# Revit family: Hager-Univers-IP30-sistema-A_parete-CH-it
name_source: partatom
category: Electrical Equipment
units: mm (PartAtom-declared; Revit-internal decimal feet)

## family parameters
Cut with Voids When Loaded = No
Host = Face
Panel Configuration = Two Columns, Circuits Across
Part Type = Panelboard
Room Calculation Point = No
Round Connector Dimension = Use Diameter
Shared = No

## types (20) — shared parameters
EF000003 - Tipo di montaggio = EV000384 - A parete
EF000007 - colore = EV000202 - bianco
EF000049 - profondità = 161 mm  [stored 0.528215 ft]
EF000116 - numero RAL = 9010
EF000118 - con piastra di montaggio = No
EF000339 - tipo di copertura = EV000494 - senza
EF001062 - esecuzione EMC = No
EF001088 - possibilità di applicazione = Yes
EF001131 - profondità interna = 161 mm  [stored 0.528215 ft]
EF001134 - barra DIN = Yes
EF001596 - Attacco Lampada = EV000179 - acciaio
EF002950 - Numero moduli DIN = 12
EF004462 - tipo di chiusura = EV000154 - altri
EF005474 - grado di protezione (IP) = EV006410 - IP30
EF006244 - coperchio/porta trasparente = No
EF006306 - con serratura = No
EF009212 - esecuzione coperchio = EV009916 - con taglio
EF015776 - Morsettiera di terra = Yes
EF015777 - Morsettiera neutra = Yes
EF015941 - Segnale di passaggio porta = No
HG000002 - Con porta = No
HG000003 - Gamma = Univers
HG000005 - Spessore = 3 mm  [stored 0.00984252 ft]
HG000006 - Ad incasso = No
HG000009 - Porta doppia a battente = No
HG000010 - Porte asimmetriche = No
HG000011 - File vuote nella parte basse = No
HG000017 - Distanza tra i poli = 18 mm  [stored 0.0590551 ft]
Manufacturer = Hager
Type Comments = Univers
zero-valued in all types: Default Elevation, EF000218 - profondità di incasso, EF000332 - Altezza della parte incassata, EF000846 - larghezza di montaggio, HG000007 - Numero di colonne vuote, HG000008 - Numero di file vuote

## per-type parameters (varying)
| type | EF000008 - Larghezza | EF000040 - Altezza | EF000266 - numero di file | HG000001 - Numero di colonne | HG000004 - Codice produttore | Model |
| A parete IP30 L1050 A1100 P161 12 Unità di divisione - FWB74T1S | 1050 mm | 1100 mm | 28 | 4 | FWB74T1S | FWB74T1S |
| A parete IP30 L1050 A500 P161 12 Unità di divisione - FWB34T1S | 1050 mm | 500 mm  [stored 1.64042 ft] | 12 | 4 | FWB34T1S | FWB34T1S |
| A parete IP30 L1050 A650 P161 12 Unità di divisione - FWB44T1S | 1050 mm | 650 mm  [stored 2.13255 ft] | 16 | 4 | FWB44T1S | FWB44T1S |
| A parete IP30 L1050 A800 P161 12 Unità di divisione - FWB54T1S | 1050 mm | 800 mm  [stored 2.62467 ft] | 20 | 4 | FWB54T1S | FWB54T1S |
| A parete IP30 L1050 A950 P161 12 Unità di divisione - FWB64T1S | 1050 mm | 950 mm  [stored 3.1168 ft] | 24 | 4 | FWB64T1S | FWB64T1S |
| A parete IP30 L300 A1100 P161 12 Unità di divisione - FWB71T1S | 300 mm | 1100 mm | 7 | 1 | FWB71T1S | FWB71T1S |
| A parete IP30 L300 A500 P161 12 Unità di divisione - FWB31T1S | 300 mm | 500 mm  [stored 1.64042 ft] | 3 | 1 | FWB31T1S | FWB31T1S |
| A parete IP30 L300 A650 P161 12 Unità di divisione - FWB41T1S | 300 mm | 650 mm  [stored 2.13255 ft] | 4 | 1 | FWB41T1S | FWB41T1S |
| A parete IP30 L300 A800 P161 12 Unità di divisione - FWB51T1S | 300 mm | 800 mm  [stored 2.62467 ft] | 5 | 1 | FWB51T1S | FWB51T1S |
| A parete IP30 L300 A950 P161 12 Unità di divisione - FWB61T1S | 300 mm | 950 mm  [stored 3.1168 ft] | 6 | 1 | FWB61T1S | FWB61T1S |
| A parete IP30 L550 A1100 P161 12 Unità di divisione - FWB72T1S | 550 mm | 1100 mm | 14 | 2 | FWB72T1S | FWB72T1S |
| A parete IP30 L550 A500 P161 12 Unità di divisione - FWB32T1S | 550 mm | 500 mm  [stored 1.64042 ft] | 6 | 2 | FWB32T1S | FWB32T1S |
| A parete IP30 L550 A650 P161 12 Unità di divisione - FWB42T1S | 550 mm | 650 mm  [stored 2.13255 ft] | 8 | 2 | FWB42T1S | FWB42T1S |
| A parete IP30 L550 A800 P161 12 Unità di divisione - FWB52T1S | 550 mm | 800 mm  [stored 2.62467 ft] | 10 | 2 | FWB52T1S | FWB52T1S |
| A parete IP30 L550 A950 P161 12 Unità di divisione - FWB62T1S | 550 mm | 950 mm  [stored 3.1168 ft] | 12 | 2 | FWB62T1S | FWB62T1S |
| A parete IP30 L800 A1100 P161 12 Unità di divisione - FWB73T1S | 800 mm  [stored 2.62467 ft] | 1100 mm | 21 | 3 | FWB73T1S | FWB73T1S |
| A parete IP30 L800 A500 P161 12 Unità di divisione - FWB33T1S | 800 mm  [stored 2.62467 ft] | 500 mm  [stored 1.64042 ft] | 9 | 3 | FWB33T1S | FWB33T1S |
| A parete IP30 L800 A650 P161 12 Unità di divisione - FWB43T1S | 800 mm  [stored 2.62467 ft] | 650 mm  [stored 2.13255 ft] | 12 | 3 | FWB43T1S | FWB43T1S |
| A parete IP30 L800 A800 P161 12 Unità di divisione - FWB53T1S | 800 mm  [stored 2.62467 ft] | 800 mm  [stored 2.62467 ft] | 15 | 3 | FWB53T1S | FWB53T1S |
| A parete IP30 L800 A950 P161 12 Unità di divisione - FWB63T1S | 800 mm  [stored 2.62467 ft] | 950 mm  [stored 3.1168 ft] | 18 | 3 | FWB63T1S | FWB63T1S |

note: [stored X ft] marks values corroborated as IEEE doubles in the binary element streams (Revit-internal decimal feet)

## geometry (parser evidence)
native form markers: Sweep x17
no freeform markers — native parametric forms only
